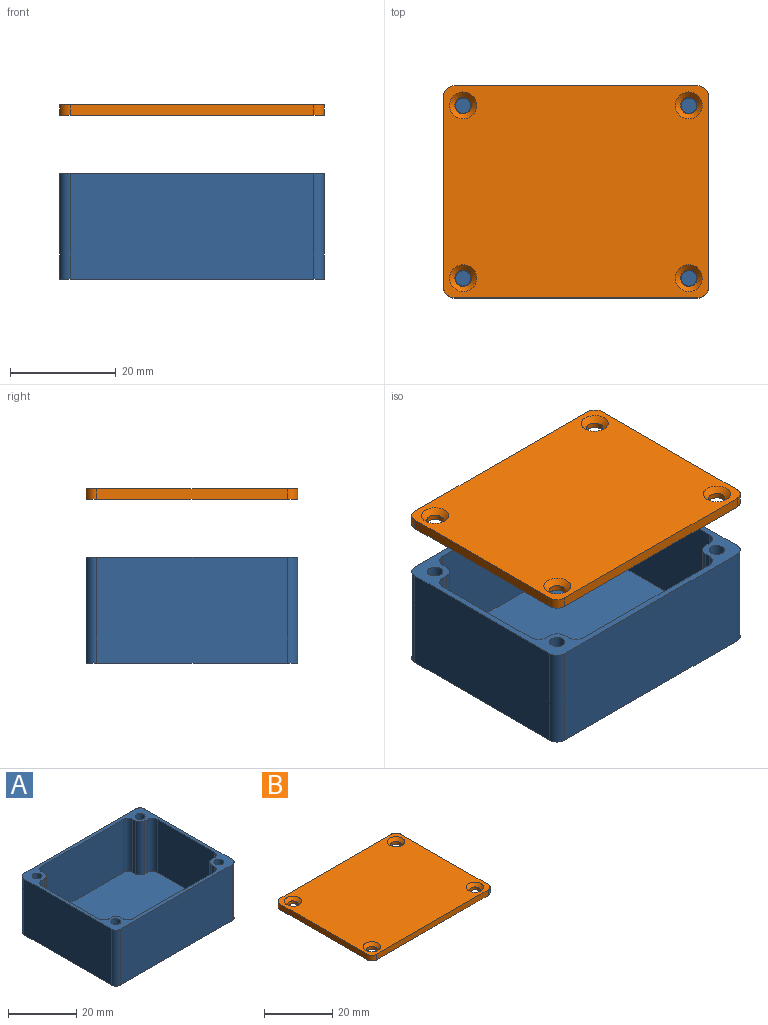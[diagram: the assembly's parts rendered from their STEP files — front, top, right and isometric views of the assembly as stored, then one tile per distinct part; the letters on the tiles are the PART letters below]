
ASSEMBLY  parts=2 mates=1
PART A: 43 faces, bbox 50x40x20 mm
  f0: plane 47.6x37.6mm, normal (0,0,1), area 1686.3mm2, adj f1,f2,f3,f4,f11,f12,f13,f14
  f1: plane 23.6x19mm, normal (1,0,0), area 448.4mm2, adj f0,f5,f33,f36
  f2: plane 33.6x19mm, normal (0,1,0), area 638.4mm2, adj f0,f5,f32,f40
  f3: plane 23.6x19mm, normal (-1,0,0), area 448.4mm2, adj f0,f5,f37,f42
  f4: plane 33.6x19mm, normal (0,-1,0), area 638.4mm2, adj f0,f5,f34,f38
  f5: plane 50x40mm, normal (0,0,1), area 283.8mm2, adj f1,f2,f3,f4,f6,f7,f8,f9
  f6: plane 46x20mm, normal (0,-1,0), area 920mm2, adj f5,f10,f27,f30
  f7: plane 36x20mm, normal (1,0,0), area 720mm2, adj f5,f10,f27,f28
  f8: plane 46x20mm, normal (0,1,0), area 920mm2, adj f5,f10,f28,f29
  f9: plane 36x20mm, normal (-1,0,0), area 720mm2, adj f5,f10,f29,f30
  f10: plane 50x40mm, normal (0,0,-1), area 1996.6mm2, adj f6,f7,f8,f9,f27,f28,f29,f30
  f11: plane 19x1mm, normal (0,-1,0), area 19mm2, adj f0,f5,f35,f36
  f12: plane 19x1mm, normal (1,0,0), area 19mm2, adj f0,f5,f34,f35
  f13: plane 19x1mm, normal (0,-1,0), area 19mm2, adj f0,f5,f37,f39
  f14: plane 19x1mm, normal (-1,0,0), area 19mm2, adj f0,f5,f38,f39
  f15: plane 19x1mm, normal (0,1,0), area 19mm2, adj f0,f5,f41,f42
  f16: plane 19x1mm, normal (-1,0,0), area 19mm2, adj f0,f5,f40,f41
  f17: plane 19x1mm, normal (0,1,0), area 19mm2, adj f0,f5,f31,f33
  f18: plane 19x1mm, normal (1,0,0), area 19mm2, adj f0,f5,f31,f32
  f19: cylinder r=1.45mm len=12mm, axis (0,0,1), area 109.3mm2, adj f5,f20
  f20: plane 2.9x2.9mm, normal (0,0,1), area 6.6mm2, adj f19
  f21: cylinder r=1.45mm len=12mm, axis (0,0,1), area 109.3mm2, adj f5,f22
  f22: plane 2.9x2.9mm, normal (0,0,1), area 6.6mm2, adj f21
  f23: cylinder r=1.45mm len=12mm, axis (0,0,1), area 109.3mm2, adj f5,f24
  f24: plane 2.9x2.9mm, normal (0,0,1), area 6.6mm2, adj f23
  f25: cylinder r=1.45mm len=12mm, axis (0,0,1), area 109.3mm2, adj f5,f26
  f26: plane 2.9x2.9mm, normal (0,0,1), area 6.6mm2, adj f25
  f27: cylinder r=2mm len=20mm, axis (0,0,1), area 62.8mm2, adj f5,f6,f7,f10
  f28: cylinder r=2mm len=20mm, axis (0,0,-1), area 62.8mm2, adj f5,f7,f8,f10
  f29: cylinder r=2mm len=20mm, axis (0,0,1), area 62.8mm2, adj f5,f8,f9,f10
  f30: cylinder r=2mm len=20mm, axis (0,0,-1), area 62.8mm2, adj f5,f6,f9,f10
  f31: cylinder r=2mm len=19mm, axis (0,0,1), area 59.7mm2, adj f0,f5,f17,f18
  f32: cylinder r=2mm len=19mm, axis (0,0,-1), area 59.7mm2, adj f0,f2,f5,f18
  f33: cylinder r=2mm len=19mm, axis (0,0,1), area 59.7mm2, adj f0,f1,f5,f17
  f34: cylinder r=2mm len=19mm, axis (0,0,-1), area 59.7mm2, adj f0,f4,f5,f12
  f35: cylinder r=2mm len=19mm, axis (0,0,1), area 59.7mm2, adj f0,f5,f11,f12
  f36: cylinder r=2mm len=19mm, axis (0,0,-1), area 59.7mm2, adj f0,f1,f5,f11
  f37: cylinder r=2mm len=19mm, axis (0,0,-1), area 59.7mm2, adj f0,f3,f5,f13
  f38: cylinder r=2mm len=19mm, axis (0,0,1), area 59.7mm2, adj f0,f4,f5,f14
  f39: cylinder r=2mm len=19mm, axis (0,0,1), area 59.7mm2, adj f0,f5,f13,f14
  f40: cylinder r=2mm len=19mm, axis (0,0,1), area 59.7mm2, adj f0,f2,f5,f16
  f41: cylinder r=2mm len=19mm, axis (0,0,1), area 59.7mm2, adj f0,f5,f15,f16
  f42: cylinder r=2mm len=19mm, axis (0,0,1), area 59.7mm2, adj f0,f3,f5,f15
PART B: 18 faces, bbox 50x40x2 mm
  f0: plane 36x2mm, normal (-1,0,0), area 72mm2, adj f8,f9,f14,f17
  f1: plane 46x2mm, normal (0,-1,0), area 92mm2, adj f8,f9,f14,f15
  f2: plane 36x2mm, normal (1,0,0), area 72mm2, adj f8,f9,f15,f16
  f3: cylinder r=1.55mm len=3.1mm, axis (0,0,-1), area 9.7mm2, adj f9,f11
  f4: cylinder r=1.55mm len=3.1mm, axis (0,0,-1), area 9.7mm2, adj f9,f12
  f5: cylinder r=1.55mm len=3.1mm, axis (0,0,-1), area 9.7mm2, adj f9,f13
  f6: plane 46x2mm, normal (0,1,0), area 92mm2, adj f8,f9,f16,f17
  f7: cylinder r=1.55mm len=3.1mm, axis (0,0,-1), area 9.7mm2, adj f9,f10
  f8: plane 50x40mm, normal (0,0,1), area 1914.9mm2, adj f0,f1,f2,f6,f10,f11,f12,f13
  f9: plane 50x40mm, normal (0,0,-1), area 1966.4mm2, adj f0,f1,f2,f3,f4,f5,f6,f7
  f10: cone r=1.55mm half-angle=45deg, axis (0,0,1), area 18.2mm2, adj f7,f8
  f11: cone r=1.55mm half-angle=45deg, axis (0,0,1), area 18.2mm2, adj f3,f8
  f12: cone r=1.55mm half-angle=45deg, axis (0,0,1), area 18.2mm2, adj f4,f8
  f13: cone r=1.55mm half-angle=45deg, axis (0,0,1), area 18.2mm2, adj f5,f8
  f14: cylinder r=2mm len=2mm, axis (0,0,1), area 6.3mm2, adj f0,f1,f8,f9
  f15: cylinder r=2mm len=2mm, axis (0,0,-1), area 6.3mm2, adj f1,f2,f8,f9
  f16: cylinder r=2mm len=2mm, axis (0,0,1), area 6.3mm2, adj f2,f6,f8,f9
  f17: cylinder r=2mm len=2mm, axis (0,0,-1), area 6.3mm2, adj f0,f6,f8,f9
PLACE A at identity fixed
PLACE B t=(-36.04,43.08,20.93)mm
MATE slider A.f21 <-> B.f7  axis (0,0,1) through (21.3,-16.3,10)mm
